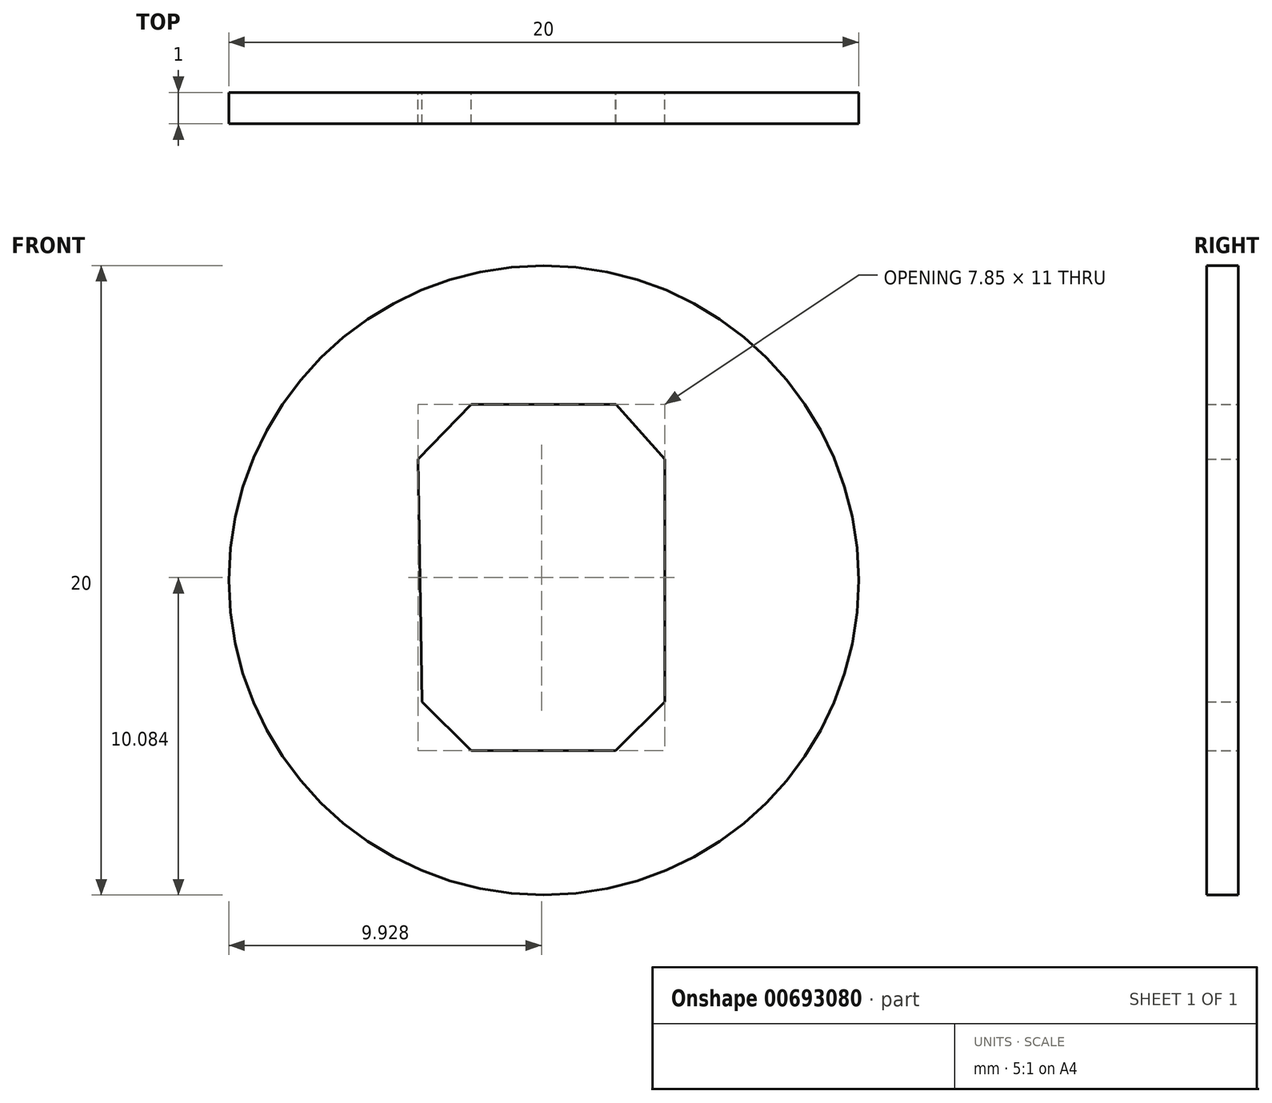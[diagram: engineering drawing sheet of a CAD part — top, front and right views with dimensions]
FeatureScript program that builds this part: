
annotation { "Feature Type Name" : "Feature", "Feature Type Description" : "" }
export const myFeature = defineFeature(function(context is Context, id is Id, definition is map)
    precondition{}
    {
        {
            var Q0;
            Q0=qCreatedBy(makeId("Front.planeOp"),FACE);
            var sketch = newSketch(context, id + "F0", { "sketchPlane" : qUnion([Q0])});
            skCircle(sketch, "E0", {"center": v(0, 0) * mm, "radius": 10 * mm});
            skSolve(sketch);
        }
        {
            var Q0;
            Q0=makeQuery(id+"F0.imprint","IMPRINT",FACE,{"disambiguationData":[TD([[makeQuery(id+"F0.imprint","IMPRINT",EDGE,{"derivedFrom":sQuery(id+"F0.wireOp",EDGE,"E0")}),1.0]])]});
            extrude(context, id + "F1", {"entities" : qUnion([Q0]), "depth" : 1 * mm, "offsetDistance" : 25 * mm});
        }
        {
            var Q0;
            Q0=qCreatedBy(makeId("Front.planeOp"),FACE);
            var sketch = newSketch(context, id + "F2", { "sketchPlane" : qUnion([Q0])});
            skLineSegment(sketch, "E1", {"start": v(0, 5.58) * mm, "end": v(2.3, 5.58) * mm});
            skLineSegment(sketch, "E2", {"start": v(0, 5.58) * mm, "end": v(-2.3, 5.58) * mm});
            skPoint(sketch, "E3.endSnap0", {"position": v(-4, 3.85) * mm});
            skLineSegment(sketch, "E4", {"start": v(-2.3, 5.58) * mm, "end": v(-4, 3.85) * mm});
            skLineSegment(sketch, "E5", {"start": v(3.85, 3.85) * mm, "end": v(2.3, 5.58) * mm});
            skLineSegment(sketch, "E6", {"start": v(-3.86, -3.85) * mm, "end": v(-2.3, -5.41) * mm});
            skLineSegment(sketch, "E7", {"start": v(3.85, -3.85) * mm, "end": v(2.29, -5.41) * mm});
            skLineSegment(sketch, "E8", {"start": v(2.29, -5.41) * mm, "end": v(-2.3, -5.41) * mm});
            skLineSegment(sketch, "E9", {"start": v(-3.86, -3.85) * mm, "end": v(-4, 3.85) * mm});
            skLineSegment(sketch, "E10", {"start": v(3.85, 3.85) * mm, "end": v(3.85, -3.85) * mm});
            skLineSegment(sketch, "E11", {"start": v(-0.42, 4.07) * mm, "end": v(-1.72, 4.07) * mm});
            skLineSegment(sketch, "E12", {"start": v(-1.72, 4.07) * mm, "end": v(-2.88, 2.88) * mm});
            skLineSegment(sketch, "E13", {"start": v(-2.88, 2.88) * mm, "end": v(-2.88, -2.88) * mm});
            skLineSegment(sketch, "E14", {"start": v(-2.88, -2.88) * mm, "end": v(-1.72, -4.01) * mm});
            skLineSegment(sketch, "E15", {"start": v(-1.72, -4.01) * mm, "end": v(-0.42, -4.01) * mm});
            skLineSegment(sketch, "E16", {"start": v(0.88, -4.01) * mm, "end": v(-0.42, -4.01) * mm});
            skSolve(sketch);
        }
        {
            var Q0;
            Q0 = qSketchRegion(id + "F2", true);
            extrude(context, id + "F3", {"entities" : qUnion([Q0]), "operationType" : NewBodyOperationType.REMOVE, "oppositeDirection" : true, "depth" : 0.7 * mm, "offsetDistance" : 25 * mm});
        }
        {
            var Q0;
            Q0=makeQuery(id+"F2.imprint","IMPRINT",FACE,{"disambiguationData":[TD([[makeQuery(id+"F2.imprint","IMPRINT",EDGE,{"derivedFrom":sQuery(id+"F2.wireOp",EDGE,"E1")}),-1.0]])]});
            extrude(context, id + "F4", {"entities" : qUnion([Q0]), "operationType" : NewBodyOperationType.REMOVE, "depth" : 1 * mm, "offsetDistance" : 25 * mm});
        }
    });
